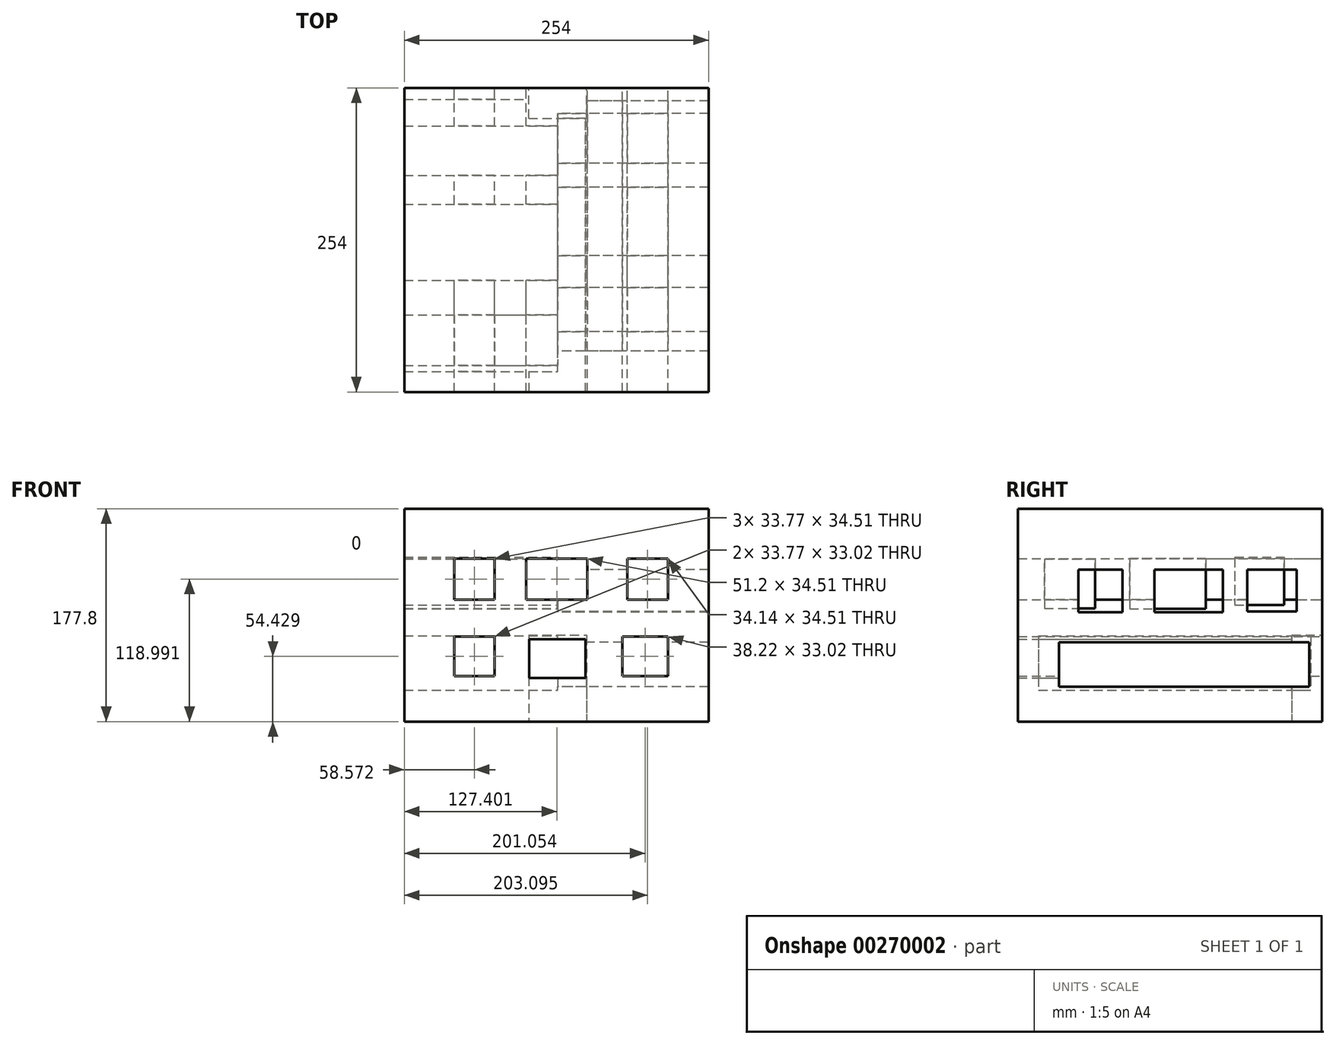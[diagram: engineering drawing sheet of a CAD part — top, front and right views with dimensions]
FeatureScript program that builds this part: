
annotation { "Feature Type Name" : "Feature", "Feature Type Description" : "" }
export const myFeature = defineFeature(function(context is Context, id is Id, definition is map)
    precondition{}
    {
        {
            var Q0;
            Q0=qCreatedBy(makeId("Front.planeOp"),FACE);
            var sketch = newSketch(context, id + "F0", { "sketchPlane" : qUnion([Q0])});
            skLineSegment(sketch, "E0.bottom", {"start": v(-128.07, 50.94) * mm, "end": v(125.93, 50.94) * mm});
            skLineSegment(sketch, "E0.top", {"start": v(-128.07, -126.86) * mm, "end": v(125.93, -126.86) * mm});
            skLineSegment(sketch, "E0.left", {"start": v(-128.07, 50.94) * mm, "end": v(-128.07, -126.86) * mm});
            skLineSegment(sketch, "E0.right", {"start": v(125.93, 50.94) * mm, "end": v(125.93, -126.86) * mm});
            skSolve(sketch);
        }
        {
            var Q0;
            Q0 = qSketchRegion(id + "F0", true);
            extrude(context, id + "F1", {"entities" : qUnion([Q0]), "depth" : 254 * mm});
        }
        {
            var Q0;
            Q0=qCreatedBy(makeId("Front.planeOp"),FACE);
            var sketch = newSketch(context, id + "F2", { "sketchPlane" : qUnion([Q0])});
            skLineSegment(sketch, "E1.bottom", {"start": v(-24.18, -54.68) * mm, "end": v(24.08, -54.68) * mm});
            skLineSegment(sketch, "E1.top", {"start": v(-24.18, -130.88) * mm, "end": v(24.08, -130.88) * mm});
            skLineSegment(sketch, "E1.left", {"start": v(-24.18, -54.68) * mm, "end": v(-24.18, -130.88) * mm});
            skLineSegment(sketch, "E1.right", {"start": v(24.08, -54.68) * mm, "end": v(24.08, -130.88) * mm});
            skLineSegment(sketch, "E2", {"start": v(0, -54.68) * mm, "end": v(0, -130.88) * mm});
            skSolve(sketch);
        }
        {
            var Q0;
            Q0 = qSketchRegion(id + "F2", true);
            extrude(context, id + "F3", {"entities" : qUnion([Q0]), "operationType" : NewBodyOperationType.REMOVE, "depth" : 25.4 * mm});
        }
        {
            var Q0;
            Q0=qCreatedBy(makeId("Front.planeOp"),FACE);
            var sketch = newSketch(context, id + "F4", { "sketchPlane" : qUnion([Q0])});
            skLineSegment(sketch, "E3.bottom", {"start": v(-52.62, -55.92) * mm, "end": v(-86.38, -55.92) * mm});
            skLineSegment(sketch, "E3.top", {"start": v(-52.62, -88.94) * mm, "end": v(-86.38, -88.94) * mm});
            skLineSegment(sketch, "E3.left", {"start": v(-52.62, -55.92) * mm, "end": v(-52.62, -88.94) * mm});
            skLineSegment(sketch, "E3.right", {"start": v(-86.38, -55.92) * mm, "end": v(-86.38, -88.94) * mm});
            skLineSegment(sketch, "E4.bottom", {"start": v(53.88, -55.92) * mm, "end": v(92.1, -55.92) * mm});
            skLineSegment(sketch, "E4.top", {"start": v(53.88, -88.94) * mm, "end": v(92.1, -88.94) * mm});
            skLineSegment(sketch, "E4.left", {"start": v(53.88, -55.92) * mm, "end": v(53.88, -88.94) * mm});
            skLineSegment(sketch, "E4.right", {"start": v(92.1, -55.92) * mm, "end": v(92.1, -88.94) * mm});
            skLineSegment(sketch, "E5.bottom", {"start": v(92.1, 9.38) * mm, "end": v(57.96, 9.38) * mm});
            skLineSegment(sketch, "E5.top", {"start": v(92.1, -25.12) * mm, "end": v(57.96, -25.12) * mm});
            skLineSegment(sketch, "E5.left", {"start": v(92.1, 9.38) * mm, "end": v(92.1, -25.12) * mm});
            skLineSegment(sketch, "E5.right", {"start": v(57.96, 9.38) * mm, "end": v(57.96, -25.12) * mm});
            skLineSegment(sketch, "E6.bottom", {"start": v(-52.62, -25.12) * mm, "end": v(-86.38, -25.12) * mm});
            skLineSegment(sketch, "E6.top", {"start": v(-52.62, 9.38) * mm, "end": v(-86.38, 9.38) * mm});
            skLineSegment(sketch, "E6.left", {"start": v(-52.62, -25.12) * mm, "end": v(-52.62, 9.38) * mm});
            skLineSegment(sketch, "E6.right", {"start": v(-86.38, -25.12) * mm, "end": v(-86.38, 9.38) * mm});
            skLineSegment(sketch, "E7.bottom", {"start": v(24.93, 9.38) * mm, "end": v(-26.27, 9.38) * mm});
            skLineSegment(sketch, "E7.top", {"start": v(24.93, -25.12) * mm, "end": v(-26.27, -25.12) * mm});
            skLineSegment(sketch, "E7.left", {"start": v(24.93, 9.38) * mm, "end": v(24.93, -25.12) * mm});
            skLineSegment(sketch, "E7.right", {"start": v(-26.27, 9.38) * mm, "end": v(-26.27, -25.12) * mm});
            skSolve(sketch);
        }
        {
            var Q0;
            Q0 = qSketchRegion(id + "F4", true);
            extrude(context, id + "F5", {"entities" : qUnion([Q0]), "operationType" : NewBodyOperationType.REMOVE, "depth" : 254 * mm});
        }
        {
            var Q0;
            Q0=qCreatedBy(makeId("Front.planeOp"),FACE);
            var sketch = newSketch(context, id + "F6", { "sketchPlane" : qUnion([Q0])});
            skLineSegment(sketch, "E8.bottom", {"start": v(-23.87, -58.02) * mm, "end": v(23.09, -58.02) * mm});
            skLineSegment(sketch, "E8.top", {"start": v(-23.87, -90.35) * mm, "end": v(23.09, -90.35) * mm});
            skLineSegment(sketch, "E8.left", {"start": v(-23.87, -58.02) * mm, "end": v(-23.87, -90.35) * mm});
            skLineSegment(sketch, "E8.right", {"start": v(23.09, -58.02) * mm, "end": v(23.09, -90.35) * mm});
            skSolve(sketch);
        }
        {
            var Q0;
            Q0 = qSketchRegion(id + "F6", true);
            extrude(context, id + "F7", {"entities" : qUnion([Q0]), "operationType" : NewBodyOperationType.REMOVE, "depth" : 508 * mm});
        }
        {
            var Q0;
            Q0=qCreatedBy(makeId("Right.planeOp"),FACE);
            var sketch = newSketch(context, id + "F8", { "sketchPlane" : qUnion([Q0])});
            skLineSegment(sketch, "E9.bottom", {"start": v(-236.92, -55.16) * mm, "end": v(-9.77, -55.16) * mm});
            skLineSegment(sketch, "E9.top", {"start": v(-236.92, -100.65) * mm, "end": v(-9.77, -100.65) * mm});
            skLineSegment(sketch, "E9.left", {"start": v(-236.92, -55.16) * mm, "end": v(-236.92, -100.65) * mm});
            skLineSegment(sketch, "E9.right", {"start": v(-9.77, -55.16) * mm, "end": v(-9.77, -100.65) * mm});
            skLineSegment(sketch, "E10.bottom", {"start": v(-232.01, 8.83) * mm, "end": v(-189.62, 8.83) * mm});
            skLineSegment(sketch, "E10.top", {"start": v(-232.01, -32.2) * mm, "end": v(-189.62, -32.2) * mm});
            skLineSegment(sketch, "E10.left", {"start": v(-232.01, 8.83) * mm, "end": v(-232.01, -32.2) * mm});
            skLineSegment(sketch, "E10.right", {"start": v(-189.62, 8.83) * mm, "end": v(-189.62, -32.2) * mm});
            skLineSegment(sketch, "E11.bottom", {"start": v(-160.94, 9.65) * mm, "end": v(-97.23, 9.65) * mm});
            skLineSegment(sketch, "E11.top", {"start": v(-160.94, -32.8) * mm, "end": v(-97.23, -32.8) * mm});
            skLineSegment(sketch, "E11.left", {"start": v(-160.94, 9.65) * mm, "end": v(-160.94, -32.8) * mm});
            skLineSegment(sketch, "E11.right", {"start": v(-97.23, 9.65) * mm, "end": v(-97.23, -32.8) * mm});
            skLineSegment(sketch, "E12.bottom", {"start": v(-73.06, 10.37) * mm, "end": v(-31.95, 10.37) * mm});
            skLineSegment(sketch, "E12.top", {"start": v(-73.06, -29.36) * mm, "end": v(-31.95, -29.36) * mm});
            skLineSegment(sketch, "E12.left", {"start": v(-73.06, 10.37) * mm, "end": v(-73.06, -29.36) * mm});
            skLineSegment(sketch, "E12.right", {"start": v(-31.95, 10.37) * mm, "end": v(-31.95, -29.36) * mm});
            skSolve(sketch);
        }
        {
            var Q0;
            Q0 = qSketchRegion(id + "F8", true);
            extrude(context, id + "F9", {"entities" : qUnion([Q0]), "operationType" : NewBodyOperationType.REMOVE, "oppositeDirection" : true, "depth" : 254 * mm});
        }
        {
            var Q0;
            Q0=qCreatedBy(makeId("Right.planeOp"),FACE);
            var sketch = newSketch(context, id + "F10", { "sketchPlane" : qUnion([Q0])});
            skLineSegment(sketch, "E13.bottom", {"start": v(-219.9, -60.61) * mm, "end": v(-10.92, -60.61) * mm});
            skLineSegment(sketch, "E13.top", {"start": v(-219.9, -97.68) * mm, "end": v(-10.92, -97.68) * mm});
            skLineSegment(sketch, "E13.left", {"start": v(-219.9, -60.61) * mm, "end": v(-219.9, -97.68) * mm});
            skLineSegment(sketch, "E13.right", {"start": v(-10.92, -60.61) * mm, "end": v(-10.92, -97.68) * mm});
            skLineSegment(sketch, "E14.bottom", {"start": v(-203.67, 0) * mm, "end": v(-166.68, 0) * mm});
            skLineSegment(sketch, "E14.top", {"start": v(-203.67, -35.48) * mm, "end": v(-166.68, -35.48) * mm});
            skLineSegment(sketch, "E14.left", {"start": v(-203.67, 0) * mm, "end": v(-203.67, -35.48) * mm});
            skLineSegment(sketch, "E14.right", {"start": v(-166.68, 0) * mm, "end": v(-166.68, -35.48) * mm});
            skLineSegment(sketch, "E15.bottom", {"start": v(-140.07, 0) * mm, "end": v(-82.96, 0) * mm});
            skLineSegment(sketch, "E15.top", {"start": v(-140.07, -35.57) * mm, "end": v(-82.96, -35.57) * mm});
            skLineSegment(sketch, "E15.left", {"start": v(-140.07, 0) * mm, "end": v(-140.07, -35.57) * mm});
            skLineSegment(sketch, "E15.right", {"start": v(-82.96, 0) * mm, "end": v(-82.96, -35.57) * mm});
            skLineSegment(sketch, "E16.bottom", {"start": v(-62.84, 0) * mm, "end": v(-21.3, 0) * mm});
            skLineSegment(sketch, "E16.top", {"start": v(-62.84, -35) * mm, "end": v(-21.3, -35) * mm});
            skLineSegment(sketch, "E16.left", {"start": v(-62.84, 0) * mm, "end": v(-62.84, -35) * mm});
            skLineSegment(sketch, "E16.right", {"start": v(-21.3, 0) * mm, "end": v(-21.3, -35) * mm});
            skSolve(sketch);
        }
        {
            var Q0;
            Q0 = qSketchRegion(id + "F10", true);
            extrude(context, id + "F11", {"entities" : qUnion([Q0]), "operationType" : NewBodyOperationType.REMOVE, "depth" : 127 * mm});
        }
    });
